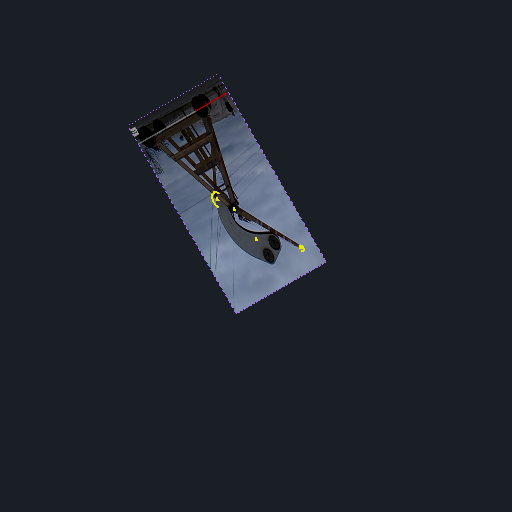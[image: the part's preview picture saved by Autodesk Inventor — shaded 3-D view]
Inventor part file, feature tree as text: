
AUTODESK INVENTOR PART (.ipt)
format: ipt  version: 2024.1 (Build 281209000, 209)  size: 406,528 bytes
history: native  units: in
note: dims shown in document units (in); Inventor stores cm internally (conversion verified against a paired STEP export)
features: other x6, reference x3, sketch x1
ambient origin geometry x8: Origin, YZ Plane, XZ Plane, XY Plane, X Axis, Y Axis, Z Axis, Center Point
feature tree (10):
  sketch  "Sketch1"
  other  "Image1"
  reference  "Reference1"
  reference  "Reference2"
  reference  "Reference3"
  other  "<userpath>\Documents\School\FallCAD\Trebuchet\Trebuchet.iam"
  other  "Trebuchet.iam"
  other  "MainArm:1"
  other  "AcrylicRod:1"
  other  "WeightArm:1"
